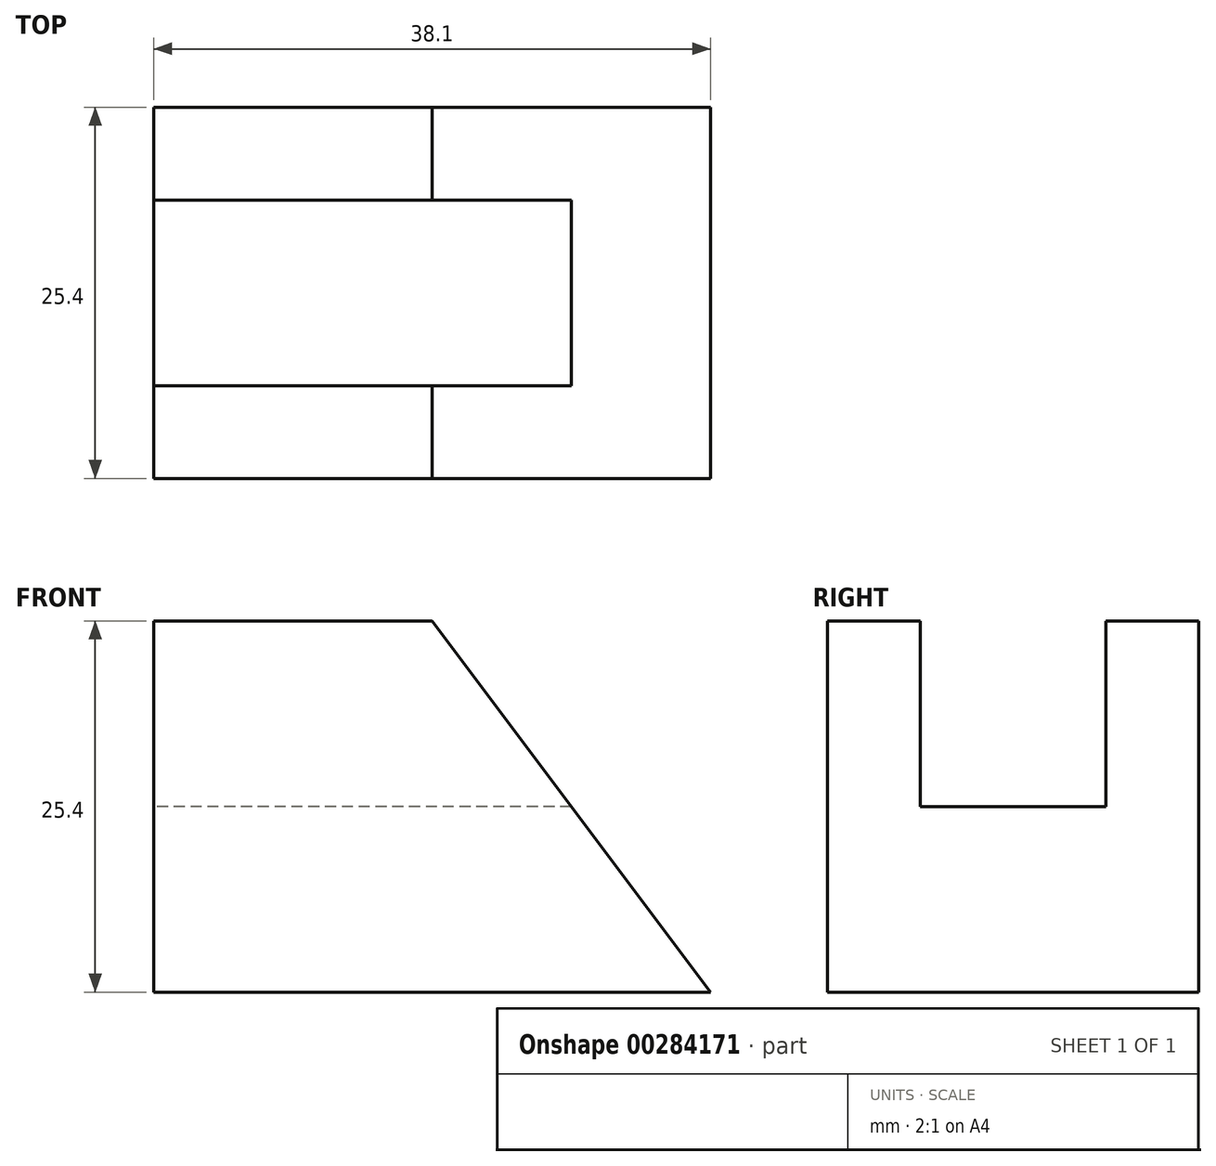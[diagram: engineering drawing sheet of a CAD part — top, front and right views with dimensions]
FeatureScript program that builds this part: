
annotation { "Feature Type Name" : "Feature", "Feature Type Description" : "" }
export const myFeature = defineFeature(function(context is Context, id is Id, definition is map)
    precondition{}
    {
        {
            var Q0;
            Q0=qCreatedBy(makeId("Front.planeOp"),FACE);
            var sketch = newSketch(context, id + "F0", { "sketchPlane" : qUnion([Q0])});
            skLineSegment(sketch, "E0", {"start": v(0, 0) * mm, "end": v(0, 25.4) * mm});
            skLineSegment(sketch, "E1", {"start": v(0, 25.4) * mm, "end": v(19.05, 25.4) * mm});
            skLineSegment(sketch, "E2", {"start": v(19.05, 25.4) * mm, "end": v(38.1, 0) * mm});
            skLineSegment(sketch, "E3", {"start": v(38.1, 0) * mm, "end": v(0, 0) * mm});
            skSolve(sketch);
        }
        {
            var Q0;
            Q0 = qSketchRegion(id + "F0", true);
            extrude(context, id + "F1", {"entities" : qUnion([Q0]), "depth" : 25.4 * mm});
        }
        {
            var Q0;
            Q0=qCreatedBy(makeId("Right.planeOp"),FACE);
            var sketch = newSketch(context, id + "F2", { "sketchPlane" : qUnion([Q0])});
            skLineSegment(sketch, "E4.bottom", {"start": v(-19.05, 25.4) * mm, "end": v(-6.35, 25.4) * mm});
            skLineSegment(sketch, "E4.top", {"start": v(-19.05, 12.7) * mm, "end": v(-6.35, 12.7) * mm});
            skLineSegment(sketch, "E4.left", {"start": v(-19.05, 25.4) * mm, "end": v(-19.05, 12.7) * mm});
            skLineSegment(sketch, "E4.right", {"start": v(-6.35, 25.4) * mm, "end": v(-6.35, 12.7) * mm});
            skSolve(sketch);
        }
        {
            var Q0;
            Q0 = qSketchRegion(id + "F2", true);
            extrude(context, id + "F3", {"entities" : qUnion([Q0]), "operationType" : NewBodyOperationType.REMOVE, "endBound" : BoundingType.THROUGH_ALL, "depth" : 25.4 * mm});
        }
    });
